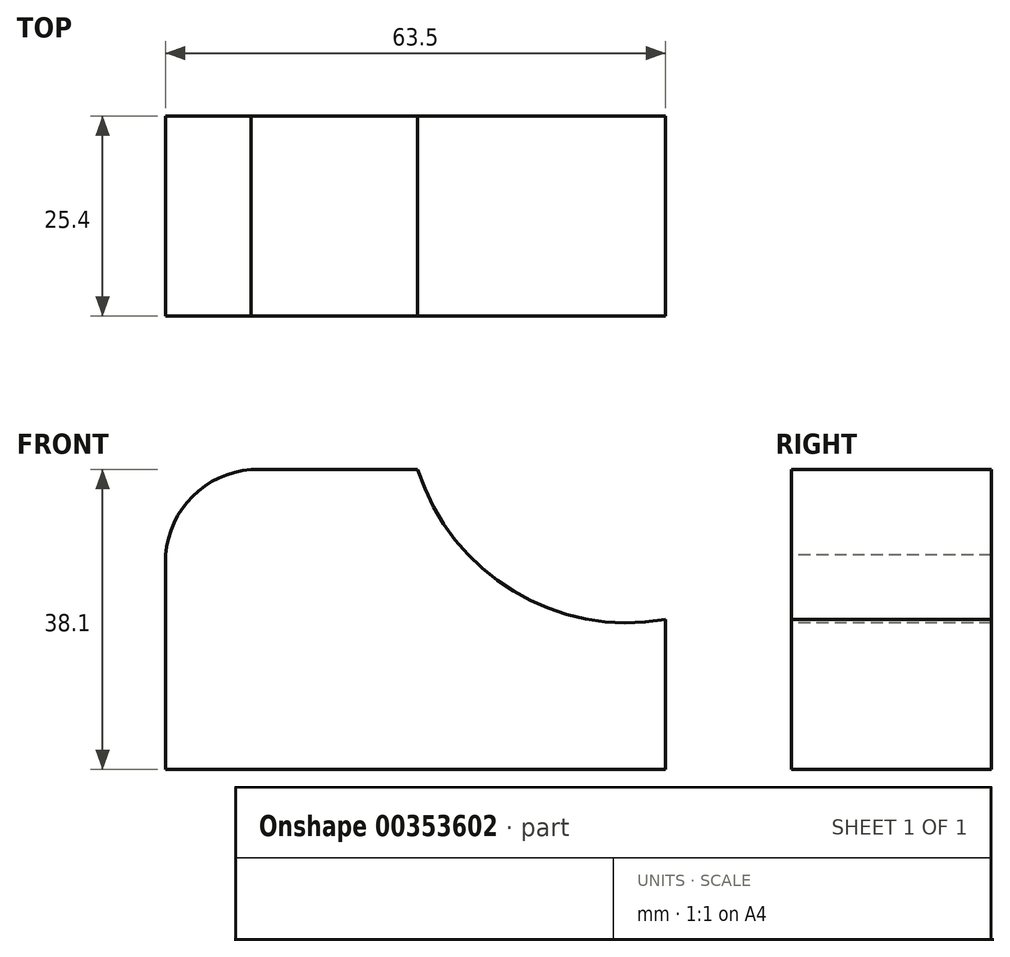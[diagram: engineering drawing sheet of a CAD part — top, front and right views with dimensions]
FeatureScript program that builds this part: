
annotation { "Feature Type Name" : "Feature", "Feature Type Description" : "" }
export const myFeature = defineFeature(function(context is Context, id is Id, definition is map)
    precondition{}
    {
        {
            var Q0;
            Q0=qCreatedBy(makeId("Front.planeOp"),FACE);
            var sketch = newSketch(context, id + "F0", { "sketchPlane" : qUnion([Q0])});
            skLineSegment(sketch, "E0", {"start": v(0, 0) * mm, "end": v(0, 38.1) * mm});
            skLineSegment(sketch, "E1", {"start": v(0, 38.1) * mm, "end": v(63.5, 38.1) * mm});
            skLineSegment(sketch, "E2", {"start": v(63.5, 38.1) * mm, "end": v(63.5, 0) * mm});
            skLineSegment(sketch, "E3", {"start": v(63.5, 0) * mm, "end": v(0, 0) * mm});
            skSolve(sketch);
        }
        {
            var Q0;
            Q0=makeQuery(id+"F0.imprint","IMPRINT",FACE,{"disambiguationData":[TD([[makeQuery(id+"F0.imprint","IMPRINT",EDGE,{"derivedFrom":sQuery(id+"F0.wireOp",EDGE,"E0")}),-1.0]])]});
            extrude(context, id + "F1", {"entities" : qUnion([Q0]), "depth" : 25.4 * mm});
        }
        {
            var Q0;
            Q0=makeQuery(id+"F1.opExtrude","CAP_FACE",FACE,{"disambiguationData":[OSD([sQuery(id+"F0.wireOp",EDGE,"E0"),sQuery(id+"F0.wireOp",EDGE,"E1"),sQuery(id+"F0.wireOp",EDGE,"E2"),sQuery(id+"F0.wireOp",EDGE,"E3")])],"isStart":false});
            var sketch = newSketch(context, id + "F2", { "sketchPlane" : qUnion([Q0])});
            skArc(sketch, "E4", {"start": v(12.7, 38.1) * mm, "mid": v(3.42, 34.68) * mm, "end": v(0, 25.4) * mm});
            skLineSegment(sketch, "E5", {"start": v(0, 25.4) * mm, "end": v(0, 38.1) * mm});
            skLineSegment(sketch, "E6", {"start": v(0, 38.1) * mm, "end": v(12.7, 38.1) * mm});
            skSolve(sketch);
        }
        {
            var Q0;
            {var subQ0=sQuery(id+"F2.wireOp",EDGE,"E6");var subQ1=sQuery(id+"F2.wireOp",EDGE,"E4");var subQ2=makeQuery(id+"F2.imprint","INTERSECT",VERTEX,{"derivedFrom":[subQ1,subQ0]});Q0=makeQuery(id+"F2.imprint","IMPRINT",FACE,{"disambiguationData":[TD([[makeQuery(id+"F2.imprint","IMPRINT",EDGE,{"disambiguationData":[TD([[subQ2,-1.0]])],"derivedFrom":subQ1}),-1.0]])]});}
            extrude(context, id + "F3", {"entities" : qUnion([Q0]), "operationType" : NewBodyOperationType.REMOVE, "oppositeDirection" : true, "depth" : 25.4 * mm});
        }
        {
            var Q0;
            Q0=makeQuery(id+"F1.opExtrude","CAP_FACE",FACE,{"disambiguationData":[OSD([sQuery(id+"F0.wireOp",EDGE,"E0"),sQuery(id+"F0.wireOp",EDGE,"E1"),sQuery(id+"F0.wireOp",EDGE,"E2"),sQuery(id+"F0.wireOp",EDGE,"E3")])],"isStart":false});
            var sketch = newSketch(context, id + "F4", { "sketchPlane" : qUnion([Q0])});
            skLineSegment(sketch, "E7", {"start": v(63.5, 38.1) * mm, "end": v(32.03, 38.1) * mm});
            skLineSegment(sketch, "E8", {"start": v(63.5, 38.1) * mm, "end": v(63.5, 19.05) * mm});
            skArc(sketch, "E9", {"start": v(32.03, 38.1) * mm, "mid": v(44.18, 22.66) * mm, "end": v(63.5, 19.05) * mm});
            skSolve(sketch);
        }
        {
            var Q0;
            Q0=makeQuery(id+"F4.imprint","IMPRINT",FACE,{"disambiguationData":[TD([[makeQuery(id+"F4.imprint","IMPRINT",EDGE,{"derivedFrom":sQuery(id+"F4.wireOp",EDGE,"E7")}),-1.0]])]});
            extrude(context, id + "F5", {"entities" : qUnion([Q0]), "operationType" : NewBodyOperationType.REMOVE, "oppositeDirection" : true, "depth" : 25.4 * mm});
        }
    });
